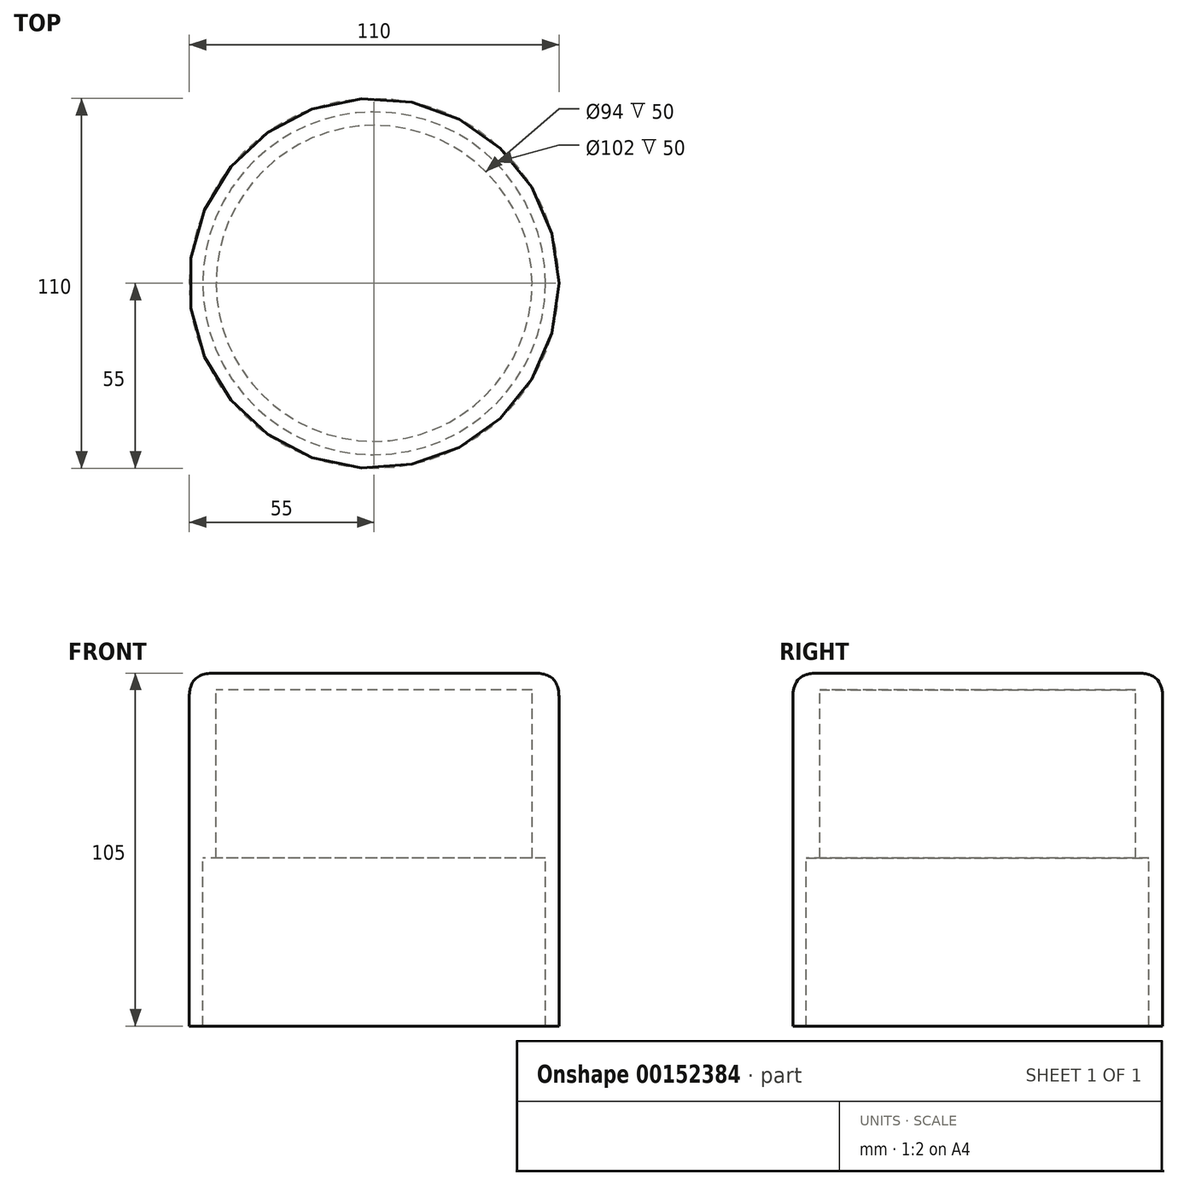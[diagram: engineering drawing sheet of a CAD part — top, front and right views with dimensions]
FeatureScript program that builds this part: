
annotation { "Feature Type Name" : "Feature", "Feature Type Description" : "" }
export const myFeature = defineFeature(function(context is Context, id is Id, definition is map)
    precondition{}
    {
        {
            var Q0;
            Q0=qCreatedBy(makeId("Top.planeOp"),FACE);
            var sketch = newSketch(context, id + "F0", { "sketchPlane" : qUnion([Q0])});
            skCircle(sketch, "E0", {"center": v(0, 0) * mm, "radius": 51 * mm});
            skCircle(sketch, "E1", {"center": v(0, 0) * mm, "radius": 55 * mm});
            skCircle(sketch, "E2", {"center": v(0, 0) * mm, "radius": 47 * mm});
            skSolve(sketch);
        }
        {
            var Q0;
            Q0=makeQuery(id+"F0.imprint","IMPRINT",FACE,{"disambiguationData":[TD([[makeQuery(id+"F0.imprint","IMPRINT",EDGE,{"derivedFrom":sQuery(id+"F0.wireOp",EDGE,"E2")}),1.0]])]});
            var Q1;
            Q1=makeQuery(id+"F0.imprint","IMPRINT",FACE,{"disambiguationData":[TD([[makeQuery(id+"F0.imprint","IMPRINT",EDGE,{"derivedFrom":sQuery(id+"F0.wireOp",EDGE,"E0")}),1.0]])]});
            var Q2;
            Q2=makeQuery(id+"F0.imprint","IMPRINT",FACE,{"disambiguationData":[TD([[makeQuery(id+"F0.imprint","IMPRINT",EDGE,{"derivedFrom":sQuery(id+"F0.wireOp",EDGE,"E0")}),-1.0]])]});
            extrude(context, id + "F1", {"entities" : qUnion([Q0, Q1, Q2]), "depth" : 5 * mm});
        }
        {
            var Q0;
            Q0=makeQuery(id+"F0.imprint","IMPRINT",FACE,{"disambiguationData":[TD([[makeQuery(id+"F0.imprint","IMPRINT",EDGE,{"derivedFrom":sQuery(id+"F0.wireOp",EDGE,"E0")}),1.0]])]});
            extrude(context, id + "F2", {"entities" : qUnion([Q0]), "operationType" : NewBodyOperationType.ADD, "oppositeDirection" : true, "depth" : 50 * mm});
        }
        {
            var Q0;
            Q0=makeQuery(id+"F0.imprint","IMPRINT",FACE,{"disambiguationData":[TD([[makeQuery(id+"F0.imprint","IMPRINT",EDGE,{"derivedFrom":sQuery(id+"F0.wireOp",EDGE,"E0")}),-1.0]])]});
            extrude(context, id + "F3", {"entities" : qUnion([Q0]), "operationType" : NewBodyOperationType.ADD, "oppositeDirection" : true, "depth" : 100 * mm});
        }
        {
            var Q0;
            Q0=makeQuery(id+"F1.opExtrude","CAP_FACE",FACE,{"disambiguationData":[OSD([sQuery(id+"F0.wireOp",EDGE,"E1")])],"isStart":false});
            fillet(context, id + "F4", {"entities" : qUnion([Q0]), "radius" : 7 * mm, "tangentPropagation" : true, "rho" : 0.5, "crossSection" : FilletCrossSection.CONIC, "allowEdgeOverflow" : false});
        }
    });
